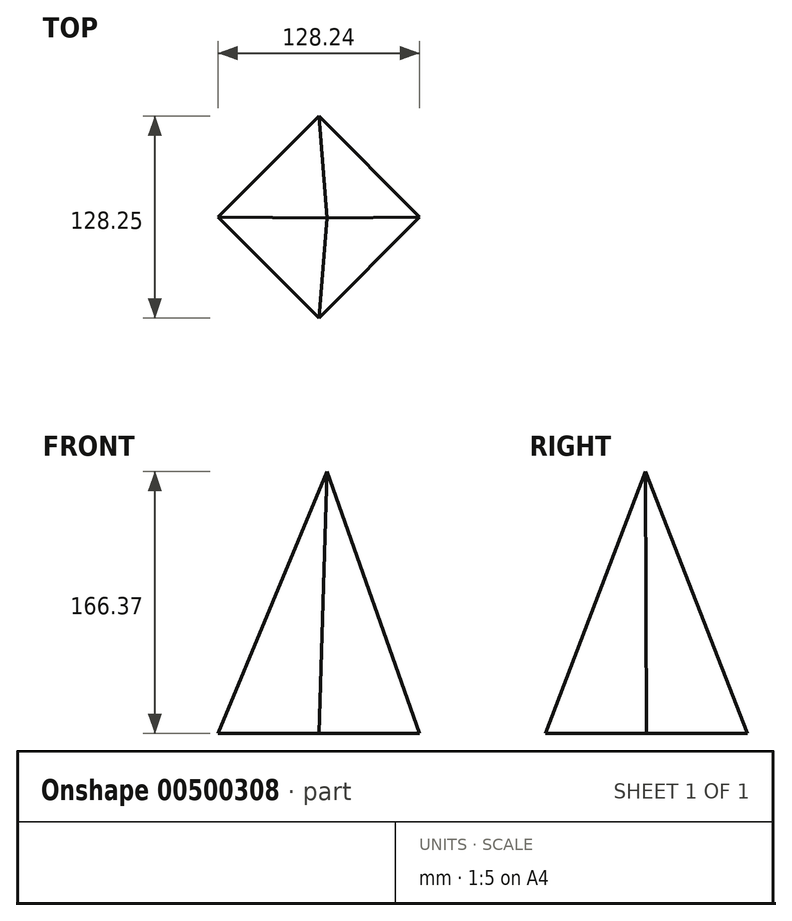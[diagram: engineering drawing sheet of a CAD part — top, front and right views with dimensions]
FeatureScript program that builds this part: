
annotation { "Feature Type Name" : "Feature", "Feature Type Description" : "" }
export const myFeature = defineFeature(function(context is Context, id is Id, definition is map)
    precondition{}
    {
        {
            var Q0;
            Q0=qCreatedBy(makeId("Top.planeOp"),FACE);
            var sketch = newSketch(context, id + "F0", { "sketchPlane" : qUnion([Q0])});
            skCircle(sketch, "E0.cCircle", {"center": v(0, 0.73) * mm, "radius": 64.12 * mm, "construction": true});
            skLineSegment(sketch, "E0.0", {"start": v(0, 64.85) * mm, "end": v(64.12, 0.73) * mm});
            skLineSegment(sketch, "E0.1", {"start": v(64.12, 0.73) * mm, "end": v(0, -63.4) * mm});
            skLineSegment(sketch, "E0.2", {"start": v(0, -63.4) * mm, "end": v(-64.12, 0.73) * mm});
            skLineSegment(sketch, "E0.3", {"start": v(-64.12, 0.73) * mm, "end": v(0, 64.85) * mm});
            skSolve(sketch);
        }
        {
            var Q0;
            Q0=qCreatedBy(makeId("Top.planeOp"),FACE);
            cPlane(context, id + "F1", {"entities" : qUnion([Q0]), "cplaneType" : CPlaneType.OFFSET, "offset" : 166.37 * mm, "width" : 152.4 * mm, "height" : 152.4 * mm});
        }
        {
            var Q0;
            Q0=qCreatedBy(id+"F1.planeOp",FACE);
            var sketch = newSketch(context, id + "F2", { "sketchPlane" : qUnion([Q0])});
            skPoint(sketch, "E1", {"position": v(5.1, 0) * mm});
            skSolve(sketch);
        }
        {
            var Q0;
            Q0=sQuery(id+"F2.wireOp",VERTEX,"E1");
            var Q1;
            Q1=makeQuery(id+"F0.imprint","IMPRINT",FACE,{"disambiguationData":[TD([[makeQuery(id+"F0.imprint","IMPRINT",EDGE,{"derivedFrom":sQuery(id+"F0.wireOp",EDGE,"E0.0")}),-1.0]])]});
            loft(context, id + "F3", {"sheetProfilesArray" : [{ "sheetProfileEntities" : qUnion([Q0]) }, { "sheetProfileEntities" : qUnion([Q1]) }]});
        }
    });
